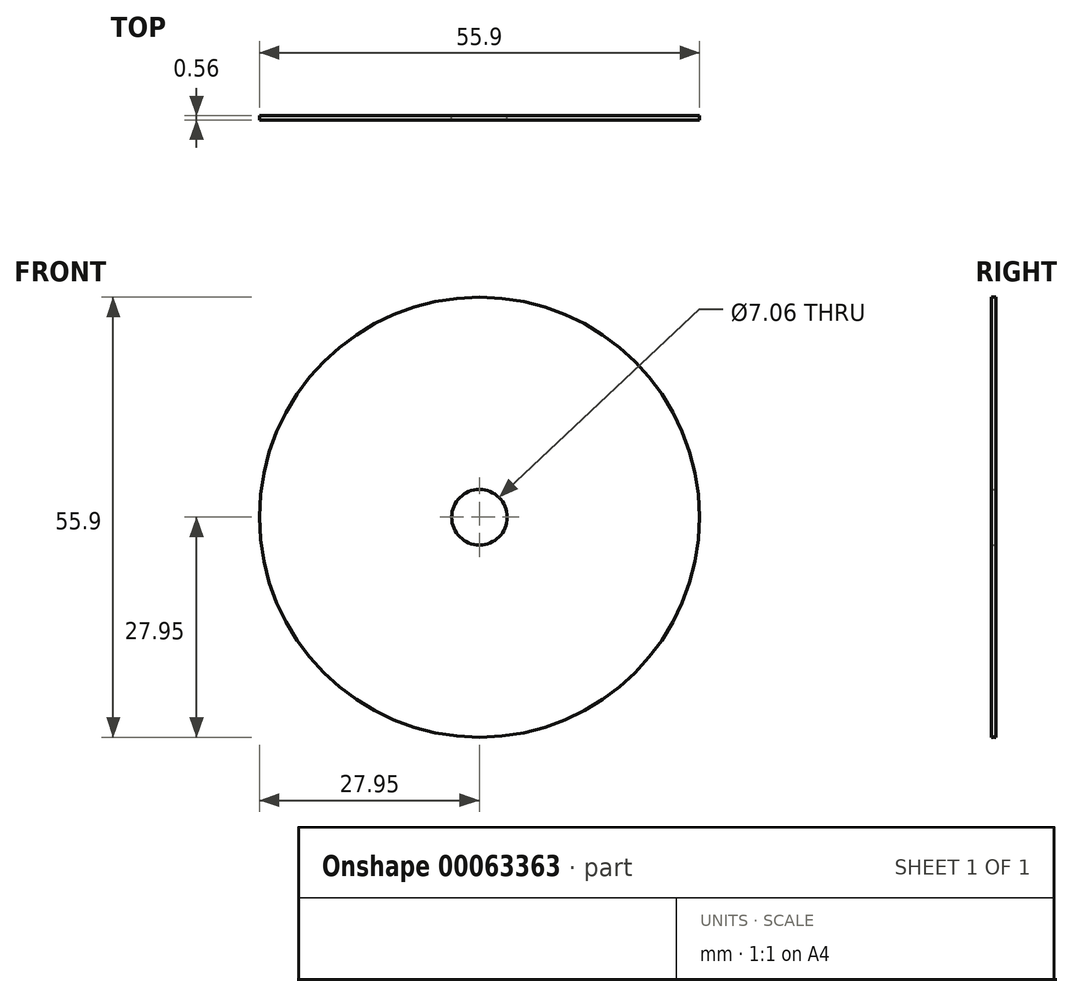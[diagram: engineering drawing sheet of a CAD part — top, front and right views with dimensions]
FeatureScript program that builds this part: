
annotation { "Feature Type Name" : "Feature", "Feature Type Description" : "" }
export const myFeature = defineFeature(function(context is Context, id is Id, definition is map)
    precondition{}
    {
        {
            assignVariable(context, id + "F0", {"name" : "D", "anyValue" : 2.5});
        }
        {
            var Q0;
            Q0=qCreatedBy(makeId("Front.planeOp"),FACE);
            var sketch = newSketch(context, id + "F1", { "sketchPlane" : qUnion([Q0])});
            skCircle(sketch, "E0", {"center": v(0, 0) * mm, "radius": 31.75 * mm});
            skSolve(sketch);
        }
        {
            var Q0;
            Q0 = qSketchRegion(id + "F1", true);
            extrude(context, id + "F2", {"entities" : qUnion([Q0]), "endBound" : BoundingType.SYMMETRIC, "depth" : (getVariable(context, 'D') / 4.5) * mm});
        }
        {
            var Q0;
            Q0=qCreatedBy(makeId("Right.planeOp"),FACE);
            var sketch = newSketch(context, id + "F3", { "sketchPlane" : qUnion([Q0])});
            skLineSegment(sketch, "E1.0", {"start": v(-7.06, -31.75) * mm, "end": v(-7.06, 31.75) * mm, "construction": true});
            skLineSegment(sketch, "E2.0", {"start": v(7.06, -31.75) * mm, "end": v(7.06, 31.75) * mm, "construction": true});
            skLineSegment(sketch, "E3", {"start": v(-12.7, 31.75) * mm, "end": v(12.7, 31.75) * mm, "construction": true});
            skArc(sketch, "E4", {"start": v(-3.81, 31.75) * mm, "mid": v(0, 27.94) * mm, "end": v(3.8, 31.75) * mm});
            skLineSegment(sketch, "E5", {"start": v(-3.81, 31.75) * mm, "end": v(3.8, 31.75) * mm});
            skSolve(sketch);
        }
        {
            var Q0;
            Q0 = qSketchRegion(id + "F3", true);
            var Q1;
            Q1=makeQuery(id+"F2.opExtrude","CAP_EDGE",EDGE,{"disambiguationData":[OSD([sQuery(id+"F1.wireOp",EDGE,"E0")])],"isStart":false});
            revolve(context, id + "F4", {"operationType" : NewBodyOperationType.REMOVE, "entities" : qUnion([Q0]), "axis" : qUnion([Q1]), "revolveType" : RevolveType.FULL, "oppositeDirection" : true});
        }
        {
            var Q0;
            Q0=makeQuery(id+"F2.opExtrude","CAP_FACE",FACE,{"disambiguationData":[OSD([sQuery(id+"F1.wireOp",EDGE,"E0")])],"isStart":true});
            var sketch = newSketch(context, id + "F5", { "sketchPlane" : qUnion([Q0])});
            skCircle(sketch, "E6", {"center": v(0, 0) * mm, "radius": 3.53 * mm});
            skSolve(sketch);
        }
        {
            var Q0;
            Q0 = qSketchRegion(id + "F5", true);
            var Q1;
            Q1=makeQuery(id+"F2.opExtrude","CAP_FACE",FACE,{"disambiguationData":[OSD([sQuery(id+"F1.wireOp",EDGE,"E0")])],"isStart":false});
            extrude(context, id + "F6", {"entities" : qUnion([Q0]), "operationType" : NewBodyOperationType.REMOVE, "endBound" : BoundingType.UP_TO_SURFACE, "oppositeDirection" : true, "endBoundEntityFace" : qUnion([Q1]), "depth" : 25.4 * mm});
        }
        {
            var Q0;
            Q0=qCreatedBy(makeId("Top.planeOp"),FACE);
            cPlane(context, id + "F7", {"entities" : qUnion([Q0]), "cplaneType" : CPlaneType.OFFSET, "offset" : 27.94 * mm, "width" : 152.4 * mm, "height" : 152.4 * mm});
        }
        {
            var Q0;
            Q0=qCreatedBy(id+"F7.planeOp",FACE);
            var sketch = newSketch(context, id + "F8", { "sketchPlane" : qUnion([Q0])});
            skCircle(sketch, "E7", {"center": v(0, 0) * mm, "radius": 0.94 * mm});
            skSolve(sketch);
        }
    });
